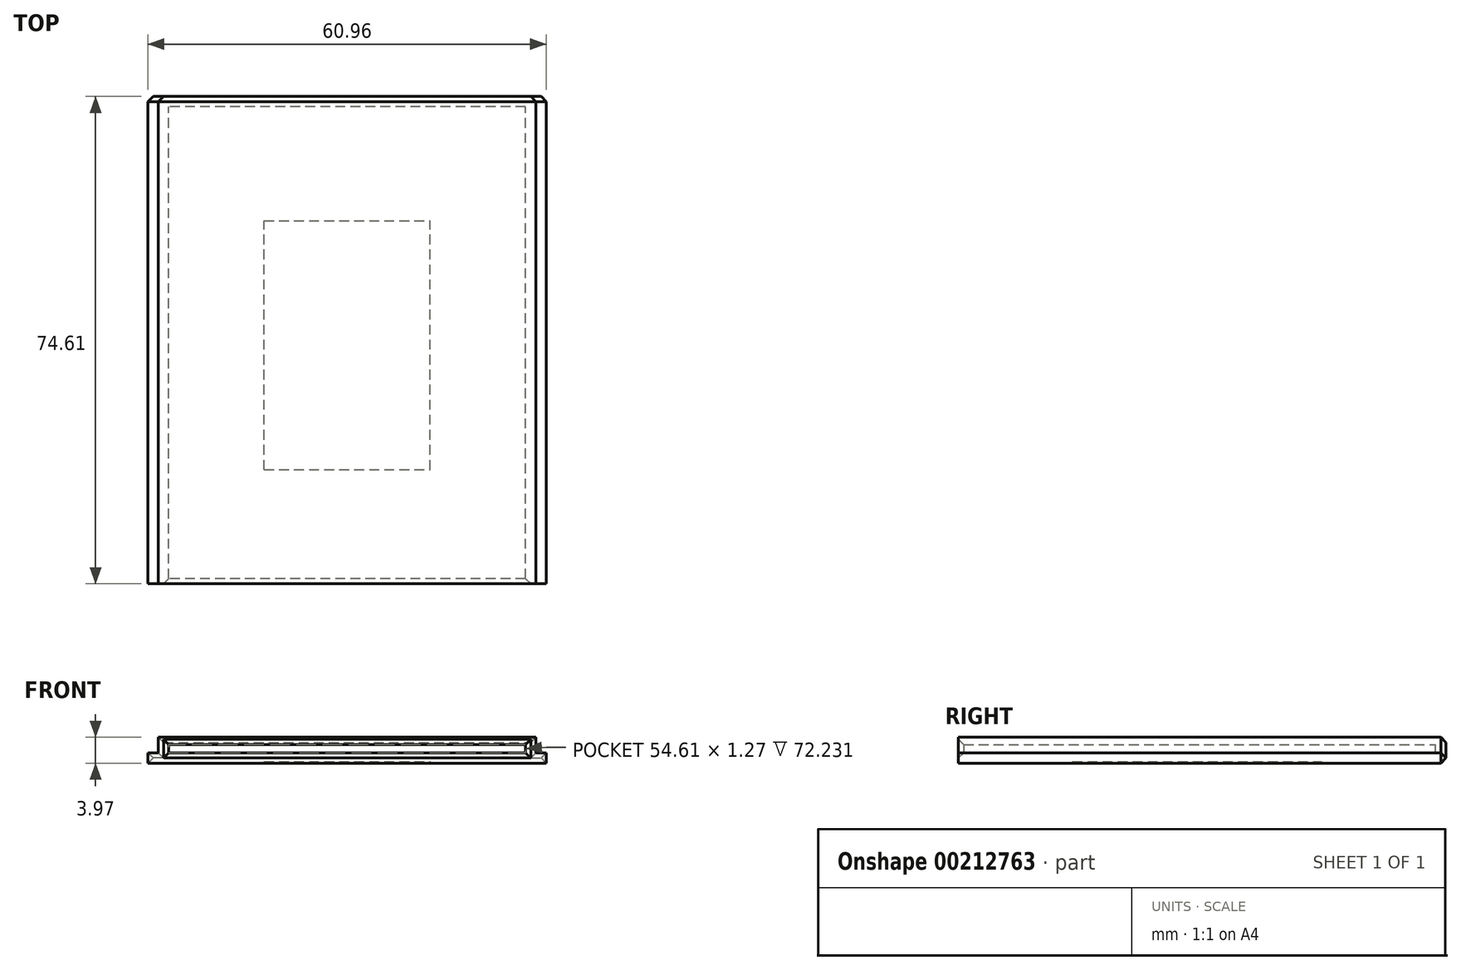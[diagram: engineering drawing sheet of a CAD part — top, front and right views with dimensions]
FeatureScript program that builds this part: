
annotation { "Feature Type Name" : "Feature", "Feature Type Description" : "" }
export const myFeature = defineFeature(function(context is Context, id is Id, definition is map)
    precondition{}
    {
        {
            var Q0;
            Q0=qCreatedBy(makeId("Front.planeOp"),FACE);
            var sketch = newSketch(context, id + "F0", { "sketchPlane" : qUnion([Q0])});
            skLineSegment(sketch, "E0", {"start": v(0, 0) * mm, "end": v(30.48, 0) * mm, "construction": true});
            skLineSegment(sketch, "E1", {"start": v(30.48, 0) * mm, "end": v(30.48, 1.59) * mm});
            skLineSegment(sketch, "E2", {"start": v(30.48, 1.59) * mm, "end": v(28.9, 1.59) * mm});
            skLineSegment(sketch, "E3", {"start": v(28.9, 1.59) * mm, "end": v(28.9, 3.97) * mm});
            skLineSegment(sketch, "E4", {"start": v(28.9, 3.97) * mm, "end": v(0, 3.97) * mm});
            skLineSegment(sketch, "E5", {"start": v(0, 3.97) * mm, "end": v(0, 0) * mm, "construction": true});
            skLineSegment(sketch, "E6.MirrorCS", {"start": v(-30.48, 1.59) * mm, "end": v(-28.9, 1.59) * mm});
            skLineSegment(sketch, "E7.MirrorCS", {"start": v(-30.48, 0) * mm, "end": v(-30.48, 1.59) * mm});
            skLineSegment(sketch, "E8.MirrorCS", {"start": v(-28.9, 1.59) * mm, "end": v(-28.9, 3.97) * mm});
            skLineSegment(sketch, "E9.MirrorCS", {"start": v(0, 0) * mm, "end": v(-30.48, 0) * mm});
            skLineSegment(sketch, "E10.MirrorCS", {"start": v(-28.9, 3.97) * mm, "end": v(0, 3.97) * mm});
            skLineSegment(sketch, "E11", {"start": v(0, 0) * mm, "end": v(27.3, 0) * mm, "construction": true});
            skLineSegment(sketch, "E12", {"start": v(27.3, 0) * mm, "end": v(0, 0) * mm});
            skLineSegment(sketch, "E13", {"start": v(0, 0) * mm, "end": v(0, 1.59) * mm});
            skLineSegment(sketch, "E14", {"start": v(0, 1.59) * mm, "end": v(27.3, 1.59) * mm});
            skLineSegment(sketch, "E15", {"start": v(27.3, 1.59) * mm, "end": v(27.3, 2.86) * mm});
            skLineSegment(sketch, "E16", {"start": v(27.3, 2.86) * mm, "end": v(0, 2.86) * mm});
            skLineSegment(sketch, "E17", {"start": v(0, 2.86) * mm, "end": v(0, 3.97) * mm});
            skLineSegment(sketch, "E18", {"start": v(0, 0) * mm, "end": v(30.48, 0) * mm});
            skLineSegment(sketch, "E19.MirrorCS", {"start": v(-27.3, 0) * mm, "end": v(0, 0) * mm});
            skLineSegment(sketch, "E20.MirrorCS", {"start": v(0, 0) * mm, "end": v(-30.48, 0) * mm, "construction": true});
            skLineSegment(sketch, "E21.MirrorCS", {"start": v(-27.3, 1.59) * mm, "end": v(-27.3, 2.86) * mm});
            skLineSegment(sketch, "E22.MirrorCS", {"start": v(0, 0) * mm, "end": v(-27.3, 0) * mm, "construction": true});
            skLineSegment(sketch, "E23.MirrorCS", {"start": v(0, 1.59) * mm, "end": v(-27.3, 1.59) * mm});
            skLineSegment(sketch, "E24.MirrorCS", {"start": v(-27.3, 2.86) * mm, "end": v(0, 2.86) * mm});
            skSolve(sketch);
        }
        {
            var Q0;
            {var subQ1=sQuery(id+"F0.wireOp",EDGE,"E1");Q0=makeQuery(id+"F0.imprint","IMPRINT",FACE,{"disambiguationData":[TD([[makeQuery(id+"F0.imprint","IMPRINT",EDGE,{"derivedFrom":subQ1}),1.0]])]});}
            var Q1;
            Q1=makeQuery(id+"F0.imprint","IMPRINT",FACE,{"disambiguationData":[TD([[makeQuery(id+"F0.imprint","IMPRINT",EDGE,{"derivedFrom":sQuery(id+"F0.wireOp",EDGE,"E6.MirrorCS")}),-1.0]])]});
            extrude(context, id + "F1", {"entities" : qUnion([Q0, Q1]), "endBound" : BoundingType.SYMMETRIC, "depth" : 73.02 * mm, "offsetDistance" : 25.4 * mm});
        }
        {
            var Q0;
            Q0=makeQuery(id+"F1.opExtrude","CAP_FACE",FACE,{"disambiguationData":[OSD([sQuery(id+"F0.wireOp",EDGE,"E1"),sQuery(id+"F0.wireOp",EDGE,"E2"),sQuery(id+"F0.wireOp",EDGE,"E3"),sQuery(id+"F0.wireOp",EDGE,"E4"),sQuery(id+"F0.wireOp",EDGE,"E6.MirrorCS"),sQuery(id+"F0.wireOp",EDGE,"E7.MirrorCS"),sQuery(id+"F0.wireOp",EDGE,"E8.MirrorCS"),sQuery(id+"F0.wireOp",EDGE,"E10.MirrorCS"),sQuery(id+"F0.wireOp",EDGE,"E13"),sQuery(id+"F0.wireOp",EDGE,"E14"),sQuery(id+"F0.wireOp",EDGE,"E15"),sQuery(id+"F0.wireOp",EDGE,"E16"),sQuery(id+"F0.wireOp",EDGE,"E18"),sQuery(id+"F0.wireOp",EDGE,"E9.MirrorCS"),sQuery(id+"F0.wireOp",EDGE,"E21.MirrorCS"),sQuery(id+"F0.wireOp",EDGE,"E23.MirrorCS"),sQuery(id+"F0.wireOp",EDGE,"E13"),sQuery(id+"F0.wireOp",EDGE,"E24.MirrorCS")])],"isStart":true});
            var sketch = newSketch(context, id + "F2", { "sketchPlane" : qUnion([Q0])});
            skLineSegment(sketch, "E25", {"start": v(-30.48, 0) * mm, "end": v(30.48, 0) * mm});
            skSolve(sketch);
        }
        {
            var Q0;
            Q0=makeQuery(id+"F2.imprint","IMPRINT",FACE,{"disambiguationData":[TD([[makeQuery(id+"F2.imprint","IMPRINT",EDGE,{"derivedFrom":makeQuery(id+"F1.opExtrude","CAP_EDGE",EDGE,{"disambiguationData":[OSD([sQuery(id+"F0.wireOp",EDGE,"E1")])],"isStart":true})}),-1.0]])]});
            var Q1;
            Q1=makeQuery(id+"F2.imprint","IMPRINT",FACE,{"disambiguationData":[TD([[makeQuery(id+"F2.imprint","IMPRINT",EDGE,{"derivedFrom":sQuery(id+"F2.wireOp",EDGE,"E25")}),1.0]])]});
            var Q2;
            Q2=makeQuery(id+"F2.imprint","IMPRINT",FACE,{"disambiguationData":[TD([[makeQuery(id+"F2.imprint","IMPRINT",EDGE,{"derivedFrom":makeQuery(id+"F1.opExtrude","CAP_EDGE",EDGE,{"disambiguationData":[OSD([sQuery(id+"F0.wireOp",EDGE,"E15")])],"isStart":true})}),-1.0]])]});
            extrude(context, id + "F3", {"entities" : qUnion([Q0, Q1, Q2]), "operationType" : NewBodyOperationType.ADD, "depth" : 1.59 * mm, "offsetDistance" : 25.4 * mm});
        }
        {
            var Q0;
            Q0=makeQuery(id+"F1.opExtrude","CAP_EDGE",EDGE,{"disambiguationData":[OSD([sQuery(id+"F0.wireOp",EDGE,"E15")])],"isStart":false});
            var Q1;
            Q1=makeQuery(id+"F1.opExtrude","CAP_EDGE",EDGE,{"disambiguationData":[OSD([sQuery(id+"F0.wireOp",EDGE,"E14"),sQuery(id+"F0.wireOp",EDGE,"E23.MirrorCS")])],"isStart":false});
            var Q2;
            Q2=makeQuery(id+"F1.opExtrude","CAP_EDGE",EDGE,{"disambiguationData":[OSD([sQuery(id+"F0.wireOp",EDGE,"E16"),sQuery(id+"F0.wireOp",EDGE,"E24.MirrorCS")])],"isStart":false});
            var Q3;
            Q3=makeQuery(id+"F1.opExtrude","CAP_EDGE",EDGE,{"disambiguationData":[OSD([sQuery(id+"F0.wireOp",EDGE,"E21.MirrorCS")])],"isStart":false});
            var Q4;
            Q4=makeQuery(id+"F3.opExtrude","CAP_EDGE",EDGE,{"disambiguationData":[OSD([sQuery(id+"F0.wireOp",EDGE,"E2")])],"isStart":false});
            var Q5;
            Q5=makeQuery(id+"F3.opExtrude","CAP_EDGE",EDGE,{"disambiguationData":[OSD([sQuery(id+"F0.wireOp",EDGE,"E3")])],"isStart":false});
            var Q6;
            Q6=makeQuery(id+"F3.opExtrude","CAP_EDGE",EDGE,{"disambiguationData":[OSD([sQuery(id+"F0.wireOp",EDGE,"E4"),sQuery(id+"F0.wireOp",EDGE,"E10.MirrorCS")])],"isStart":false});
            var Q7;
            Q7=makeQuery(id+"F3.opExtrude","CAP_EDGE",EDGE,{"disambiguationData":[OSD([sQuery(id+"F2.wireOp",EDGE,"E25")])],"isStart":false});
            var Q8;
            Q8=makeQuery(id+"F3.opExtrude","CAP_EDGE",EDGE,{"disambiguationData":[OSD([sQuery(id+"F0.wireOp",EDGE,"E1")])],"isStart":false});
            var Q9;
            Q9=makeQuery(id+"F3.opExtrude","CAP_EDGE",EDGE,{"disambiguationData":[OSD([sQuery(id+"F0.wireOp",EDGE,"E8.MirrorCS")])],"isStart":false});
            var Q10;
            Q10=makeQuery(id+"F3.opExtrude","CAP_EDGE",EDGE,{"disambiguationData":[OSD([sQuery(id+"F0.wireOp",EDGE,"E6.MirrorCS")])],"isStart":false});
            var Q11;
            Q11=makeQuery(id+"F3.opExtrude","CAP_EDGE",EDGE,{"disambiguationData":[OSD([sQuery(id+"F0.wireOp",EDGE,"E7.MirrorCS")])],"isStart":false});
            chamfer(context, id + "F4", {"entities" : qUnion([Q0, Q1, Q2, Q3, Q4, Q5, Q6, Q7, Q8, Q9, Q10, Q11]), "width" : 0.8 * mm});
        }
        {
            var Q0;
            Q0=makeQuery(id+"F3.boolean.opBoolean","MERGE",FACE,{"derivedFrom":[makeQuery(id+"F1.opExtrude","SWEPT_FACE",FACE,{"disambiguationData":[OSD([sQuery(id+"F0.wireOp",EDGE,"E18"),sQuery(id+"F0.wireOp",EDGE,"E9.MirrorCS")])]}),makeQuery(id+"F3.opExtrude","SWEPT_FACE",FACE,{"disambiguationData":[OSD([sQuery(id+"F2.wireOp",EDGE,"E25")])]})]});
            var sketch = newSketch(context, id + "F5", { "sketchPlane" : qUnion([Q0])});
            skLineSegment(sketch, "E26.bottom", {"start": v(-12.7, 19.05) * mm, "end": v(12.7, 19.05) * mm});
            skLineSegment(sketch, "E26.top", {"start": v(-12.7, -19.05) * mm, "end": v(12.7, -19.05) * mm});
            skLineSegment(sketch, "E26.left", {"start": v(-12.7, 19.05) * mm, "end": v(-12.7, -19.05) * mm});
            skLineSegment(sketch, "E26.right", {"start": v(12.7, 19.05) * mm, "end": v(12.7, -19.05) * mm});
            skPoint(sketch, "E26.middle", {"position": v(0, 0) * mm});
            skSolve(sketch);
        }
        {
            var Q0;
            Q0=makeQuery(id+"F5.imprint","IMPRINT",FACE,{"disambiguationData":[TD([[makeQuery(id+"F5.imprint","IMPRINT",EDGE,{"derivedFrom":sQuery(id+"F5.wireOp",EDGE,"E26.bottom")}),-1.0]])]});
            extrude(context, id + "F6", {"entities" : qUnion([Q0]), "operationType" : NewBodyOperationType.REMOVE, "oppositeDirection" : true, "depth" : 0.25 * mm, "offsetDistance" : 25.4 * mm});
        }
    });
